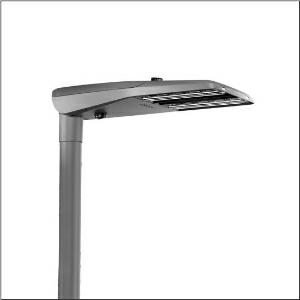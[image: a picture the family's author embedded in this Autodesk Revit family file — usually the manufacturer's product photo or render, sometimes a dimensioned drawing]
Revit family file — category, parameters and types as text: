
# Revit family: streetlight_sl_11_iq_midi___st1_2a_5xc3a51y08le_7352
name_source: partatom
category: Lighting Fixtures
units: mm (PartAtom-declared; Revit-internal decimal feet)

## family parameters
Cut with Voids When Loaded = No
Host = Face
Light Source = No
Part Type = Normal
Room Calculation Point = No
Round Connector Dimension = Use Diameter
Shared = No

## types (1)
- --- (1 x LED, 9210 lm, 59.4 W, 3000K)
    Apparent Load = 59 VA
    CIE Flux Codes = 32 70 96 100 100
    Color Rendering = 70
    Color Temperature = 3000K
    Default Elevation = 1800 mm
    Description = Streetlight SL 11 iQ midi, mast luminaire, primary light control with 3 zone facetted reflector, of plastic, silver coated, highly specular, primary optical cover: cover, of PMMA, transparent, light distribution: ST1.2a, light emission: direct distribution, primary light characteristic: asymmetric, installation type: post-top, side-entry, lamps: LED, High Power LED, rated values: 9.210lm | 59,4W | 155,1lm/W (begin service life); end service life: 9.210lm | 61,6W; at 50% lumin. flux: 4.605lm | 28,5W | 161,6lm/W, colour temperature: 3000K, colour rendering: CRI > 70, light colour: 730, light setting 1 begin service life: 100% | 9.210lm | 59,4W | 155,1lm/W | 3.000K, light setting 1 end service life: 61,6W, further light settings possible, control: pre-setting: logarithmic dimming characteristic, Street-Remote, Auto-Match, Temp-Guard, Lumen-Switch, Night-Set, Smart-Wire, Light-Fading, Desk-Remote (wireless, voltage-free reading and setting of iQ features in the workshop via application-optimized NFC function/RFID function), optimised constant luminous flux control (CLO 2.0), with cable H07RN-F 5x 1.5mm², mains connection: 230..240V, AC, 50/60Hz, connection cable pre-assembled, cable length: 8,5m, luminaire housing, of diecast aluminium, powder-coated, Siteco® metallic grey (DB 702S), please order mast flange separately, inclination adjustable without tools: 0°, 5°, 10°, 15° (post-top) | 0°, -5°, -10°, -15° (side-entry), sealing non-destructively replaceable, multi-level sealing system, length: 780mm, width: 376mm, height: 118mm, mast flange for spigot size: 42mm (side-entry): 5XC10008XM4, 60/48mm (side-entry/post-top): 5XC10108XM2, 76/60mm (side-entry/post-top): 5XC10108XM1, equipment: standard, Smart Interface below and above, protection rating (complete): IP66, insulation class (complete): insulation class II (safety insulation), certification: CE, ENEC, ENEC+, VDE, UKCA, impact resistance: IK10, permissible operating ambient temperature for outdoor applications: -25..+50°C, standard-compliant lighting for roads and squares, Environmental Product Declaration (EPD) tested and certified by an independent institute, packaging unit: 1 piece

Light Distribution: ST1.2a
    Height = 118 mm
    Lamp = 1 x LED
    Lamp Light Flux = 9210 lm
    Lamp Power = 59.4 W
    Lamp count = 1
    Length = 780 mm
    Luminous efficacy = 155 lm/W
    Manufacturer = Siteco
    ModVariant = No
    Model = 5XC3A51Y08LE
    Number of Poles = 1
    OnlyDefault = Yes
    Power Factor = 1
    Product Name = Streetlight SL 11 iQ midi | ST1.2a
    Product group = mast luminaire | pylon top
    ProductGroupID = 6100
    Protection Class = Protection class II
    Protection Degree = IP 66
    RLX_Detail_Level = 1
    RLX_Emergency_Light_Flux = 0 lm
    RLX_Emergency_Type = 0
    RLX_Emergency_Type_DB = No
    RlxData = <blob elided: 69949 chars, md5=a8943a5c>
    Socket = socket
    Standby Power = 0 W
    System Light Flux = 9210 lm
    System Power = 59 W
    Type Comments = factory setting: luminous flux: 100 % | dim-lin: 254 | 521 mA
    Type Image = l_1004429.jpg
    URL = http://relux.com
    VarID = @adj_154783
    Voltage = 0 V
    Weight = 0.00 kg
    Width = 376 mm

## geometry (parser evidence)
native form markers: Blend x4, Sweep x9
no freeform markers — native parametric forms only
